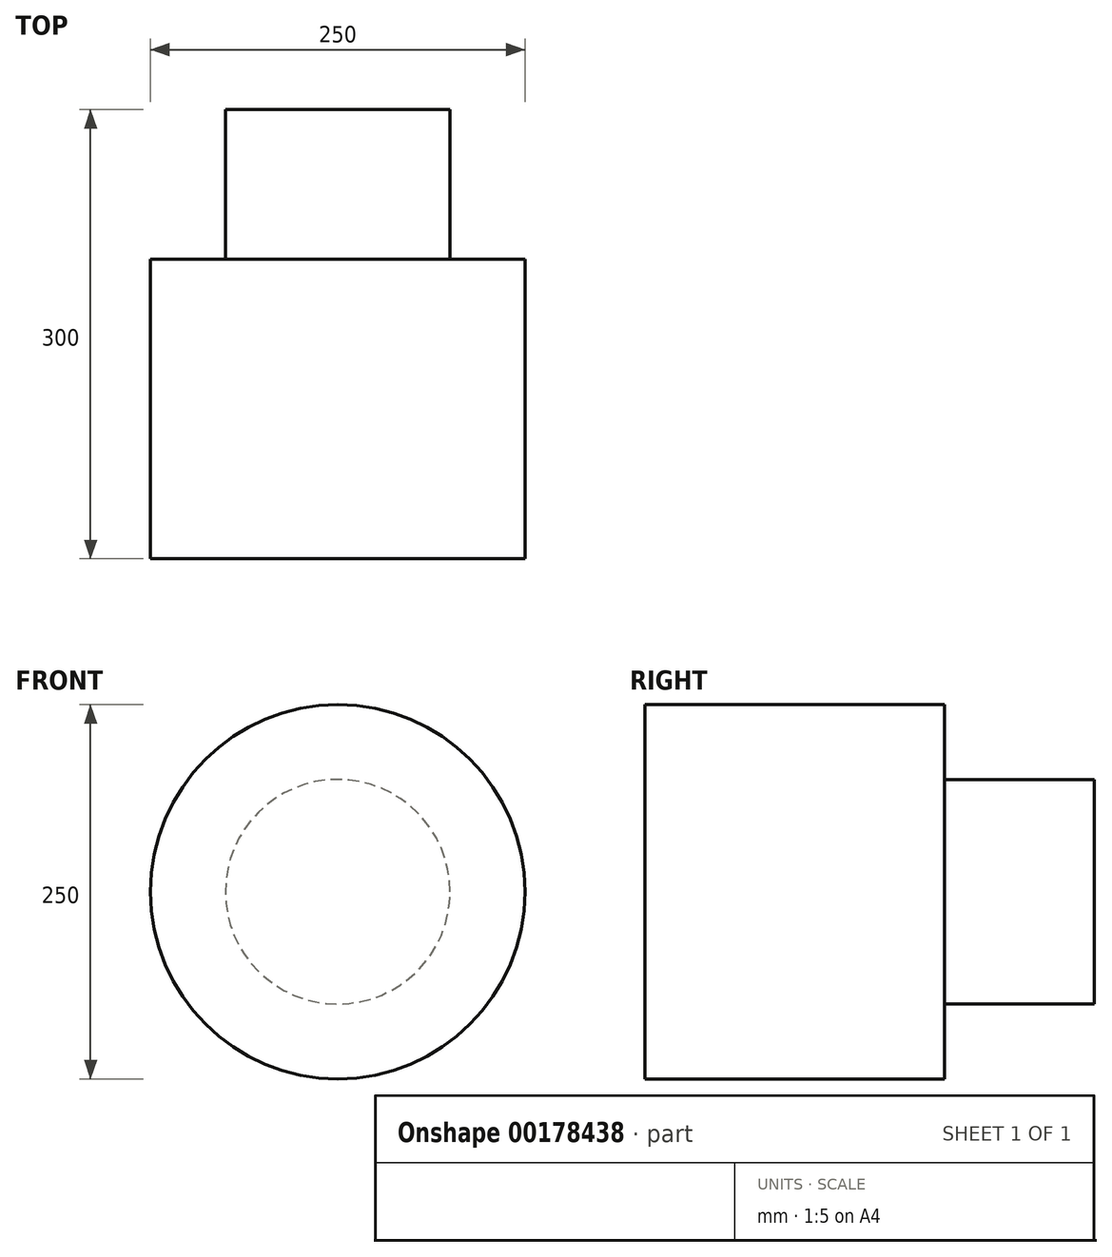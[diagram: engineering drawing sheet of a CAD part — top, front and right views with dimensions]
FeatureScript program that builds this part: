
annotation { "Feature Type Name" : "Feature", "Feature Type Description" : "" }
export const myFeature = defineFeature(function(context is Context, id is Id, definition is map)
    precondition{}
    {
        {
            var Q0;
            Q0=qCreatedBy(makeId("Front.planeOp"),FACE);
            var sketch = newSketch(context, id + "F0", { "sketchPlane" : qUnion([Q0])});
            skCircle(sketch, "E0", {"center": v(0, 0) * mm, "radius": 125 * mm});
            skSolve(sketch);
        }
        {
            var Q0;
            Q0 = qSketchRegion(id + "F0", true);
            var Q1;
            Q1=makeQuery(id+"F0.imprint","IMPRINT",FACE,{"disambiguationData":[TD([[makeQuery(id+"F0.imprint","IMPRINT",EDGE,{"derivedFrom":sQuery(id+"F0.wireOp",EDGE,"E0")}),1.0]])]});
            extrude(context, id + "F1", {"entities" : qUnion([Q0, Q1]), "depth" : 200 * mm});
        }
        {
            var Q0;
            Q0=qCreatedBy(makeId("Front.planeOp"),FACE);
            var sketch = newSketch(context, id + "F2", { "sketchPlane" : qUnion([Q0])});
            skCircle(sketch, "E1", {"center": v(0, 0) * mm, "radius": 75 * mm});
            skSolve(sketch);
        }
        {
            var Q0;
            Q0 = qSketchRegion(id + "F2", true);
            extrude(context, id + "F3", {"entities" : qUnion([Q0]), "operationType" : NewBodyOperationType.ADD, "depth" : 25 * mm, "hasSecondDirection" : true, "secondDirectionOppositeDirection" : true, "secondDirectionDepth" : 100 * mm});
        }
    });
